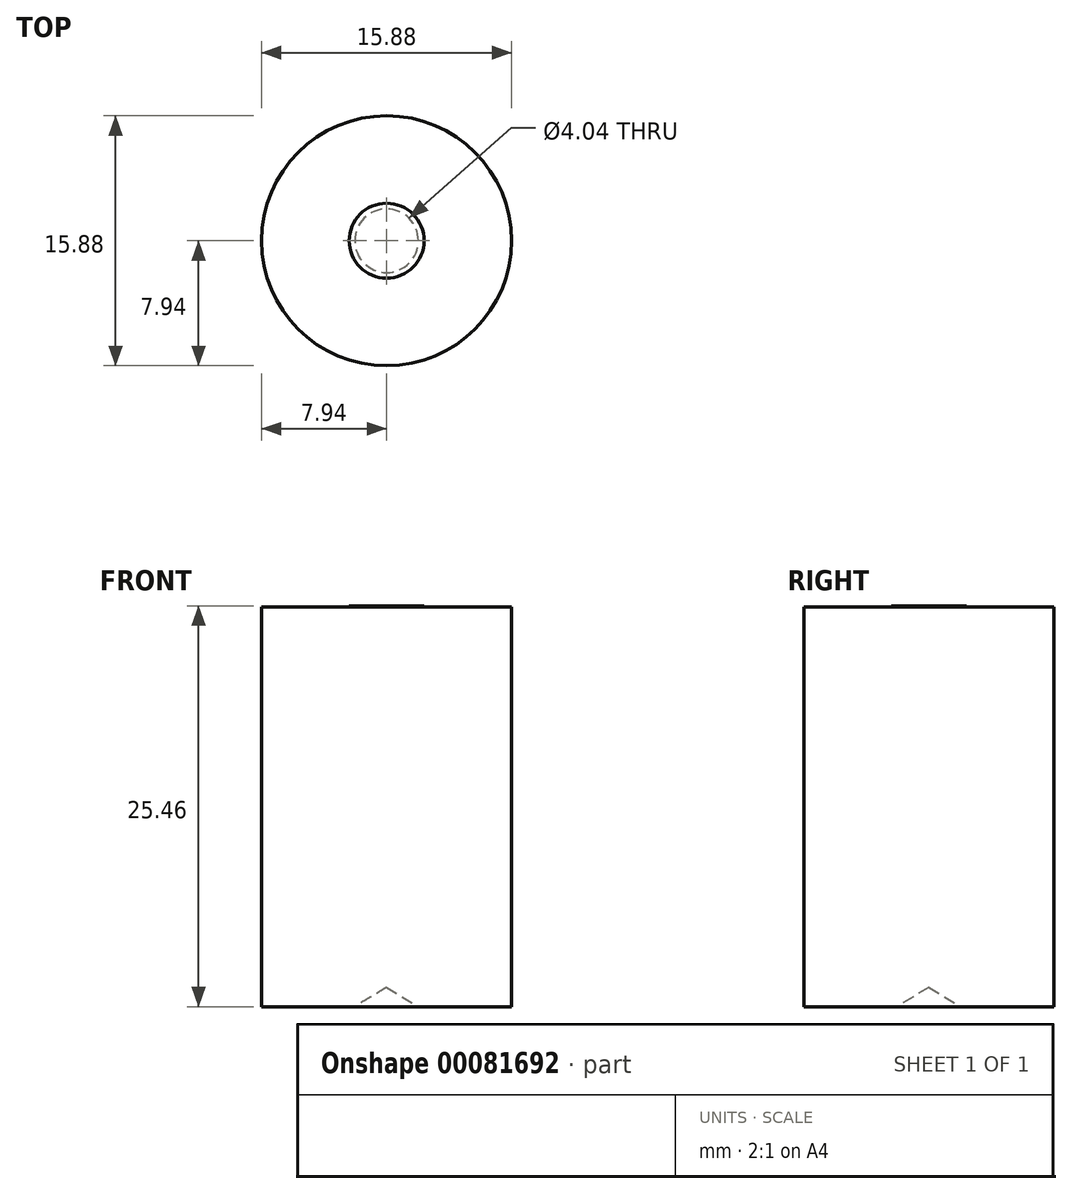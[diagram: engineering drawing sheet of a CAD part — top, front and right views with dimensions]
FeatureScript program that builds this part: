
annotation { "Feature Type Name" : "Feature", "Feature Type Description" : "" }
export const myFeature = defineFeature(function(context is Context, id is Id, definition is map)
    precondition{}
    {
        {
            var Q0;
            Q0=qCreatedBy(makeId("Top.planeOp"),FACE);
            var sketch = newSketch(context, id + "F0", { "sketchPlane" : qUnion([Q0])});
            skCircle(sketch, "E0", {"center": v(0, 0) * mm, "radius": 7.94 * mm});
            skSolve(sketch);
        }
        {
            var Q0;
            Q0=makeQuery(id+"F0.imprint","IMPRINT",FACE,{"disambiguationData":[TD([[makeQuery(id+"F0.imprint","IMPRINT",EDGE,{"derivedFrom":sQuery(id+"F0.wireOp",EDGE,"E0")}),1.0]])]});
            extrude(context, id + "F1", {"entities" : qUnion([Q0]), "depth" : 25.4 * mm});
        }
        {
            var Q0;
            Q0=makeQuery(id+"F1.opExtrude","CAP_FACE",FACE,{"disambiguationData":[OSD([sQuery(id+"F0.wireOp",EDGE,"E0")])],"isStart":false});
            var sketch = newSketch(context, id + "F2", { "sketchPlane" : qUnion([Q0])});
            skCircle(sketch, "E1", {"center": v(0, 0) * mm, "radius": 2.38 * mm});
            skSolve(sketch);
        }
        {
            var Q0;
            Q0=makeQuery(id+"F1.opExtrude","CAP_FACE",FACE,{"disambiguationData":[OSD([sQuery(id+"F0.wireOp",EDGE,"E0")])],"isStart":true});
            var sketch = newSketch(context, id + "F3", { "sketchPlane" : qUnion([Q0])});
            skPoint(sketch, "E2", {"position": v(0, 0) * mm});
            skSolve(sketch);
        }
        {
            var Q0;
            Q0=sQuery(id+"F3.wireOp",VERTEX,"E2");
            var Q1;
            Q1=makeQuery(id+"F1.opExtrude","SWEPT_BODY",BODY,{"disambiguationData":[OSD([sQuery(id+"F0.wireOp",EDGE,"E0")])]});
            hole(context, id + "F4", {"style" : HoleStyle.SIMPLE, "endStyle" : HoleEndStyle.BLIND, "standardTappedOrClearance" : lookupTablePath({ "standard" : "ANSI", "engagement" : "75%", "pitch" : "32 tpi", "size" : "#10", "type" : "Tapped" }), "standardBlindInLast" : lookupTablePath({ "standard" : "ANSI", "engagement" : "75%", "pitch" : "32 tpi", "size" : "#10", "type" : "Tapped" }), "holeDiameter" : 4.04 * mm, "holeDepth" : 3 / 203.2 * mm, "locations" : qUnion([Q0]), "scope" : qUnion([Q1]), "majorDiameter" : 4.83 * mm});
        }
        {
            var Q0;
            Q0=makeQuery(id+"F2.imprint","IMPRINT",FACE,{"disambiguationData":[TD([[makeQuery(id+"F2.imprint","IMPRINT",EDGE,{"derivedFrom":sQuery(id+"F2.wireOp",EDGE,"E1")}),1.0]])]});
            extrude(context, id + "F5", {"entities" : qUnion([Q0]), "operationType" : NewBodyOperationType.ADD, "depth" : 0.06 * mm});
        }
    });
